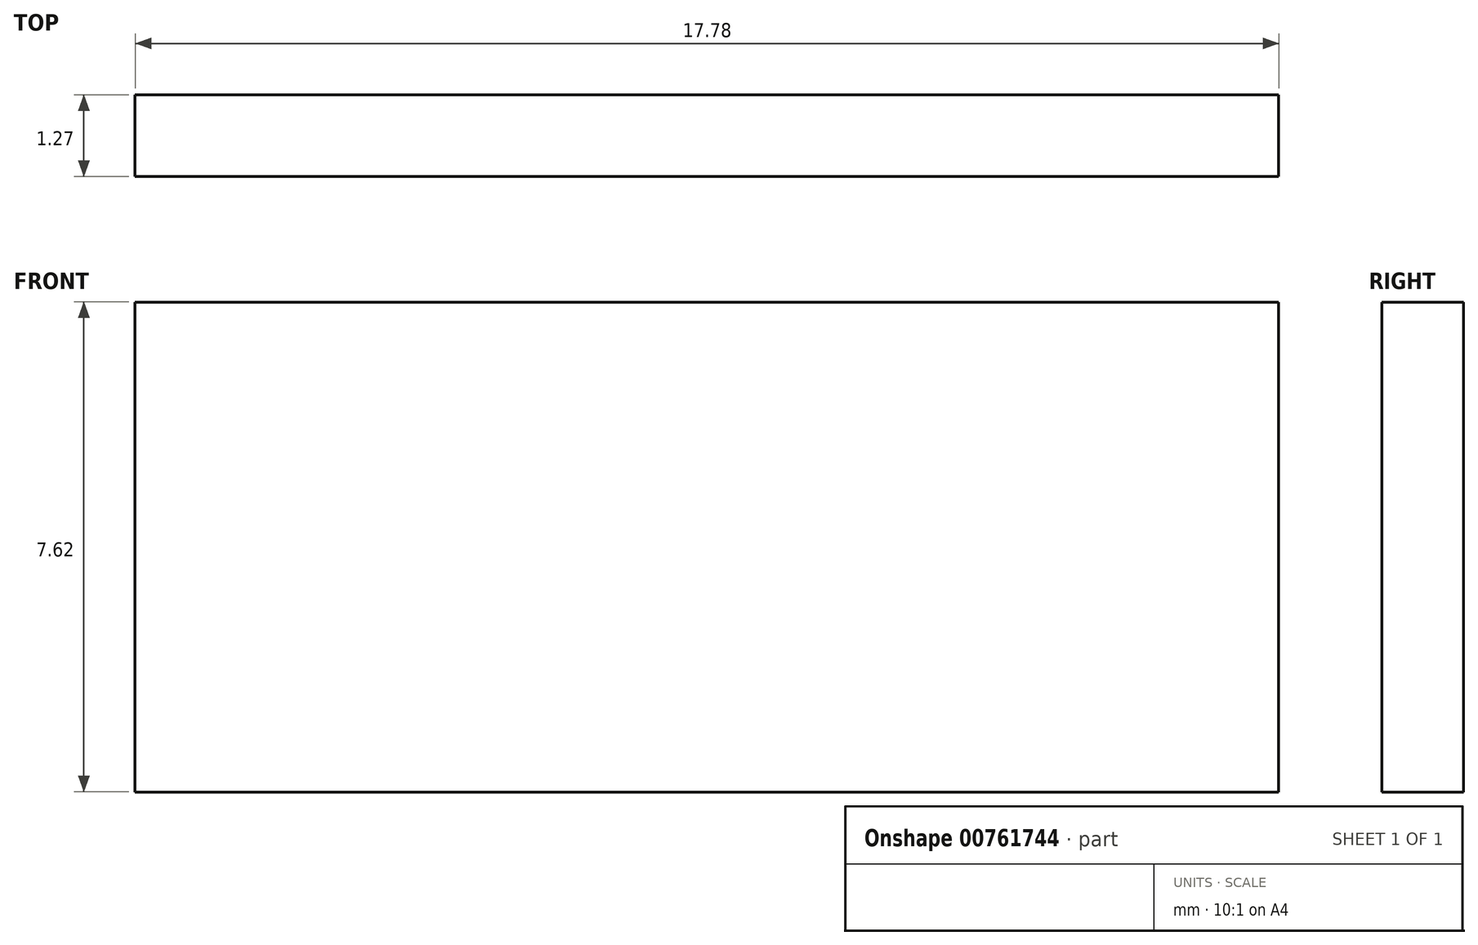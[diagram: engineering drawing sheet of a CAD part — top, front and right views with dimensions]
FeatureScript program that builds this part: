
annotation { "Feature Type Name" : "Feature", "Feature Type Description" : "" }
export const myFeature = defineFeature(function(context is Context, id is Id, definition is map)
    precondition{}
    {
        {
            var Q0;
            Q0=qCreatedBy(makeId("Front.planeOp"),FACE);
            var sketch = newSketch(context, id + "F0", { "sketchPlane" : qUnion([Q0])});
            skLineSegment(sketch, "E0.bottom", {"start": v(-53, 26.64) * mm, "end": v(-35.21, 26.64) * mm});
            skLineSegment(sketch, "E0.top", {"start": v(-53, 19.02) * mm, "end": v(-35.21, 19.02) * mm});
            skLineSegment(sketch, "E0.left", {"start": v(-53, 26.64) * mm, "end": v(-53, 19.02) * mm});
            skLineSegment(sketch, "E0.right", {"start": v(-35.21, 26.64) * mm, "end": v(-35.21, 19.02) * mm});
            skSolve(sketch);
        }
        {
            var Q0;
            Q0=makeQuery(id+"F0.imprint","IMPRINT",FACE,{"disambiguationData":[TD([[makeQuery(id+"F0.imprint","IMPRINT",EDGE,{"derivedFrom":sQuery(id+"F0.wireOp",EDGE,"E0.bottom")}),-1.0]])]});
            extrude(context, id + "F1", {"entities" : qUnion([Q0]), "depth" : 1.27 * mm, "offsetDistance" : 25.4 * mm});
        }
    });
